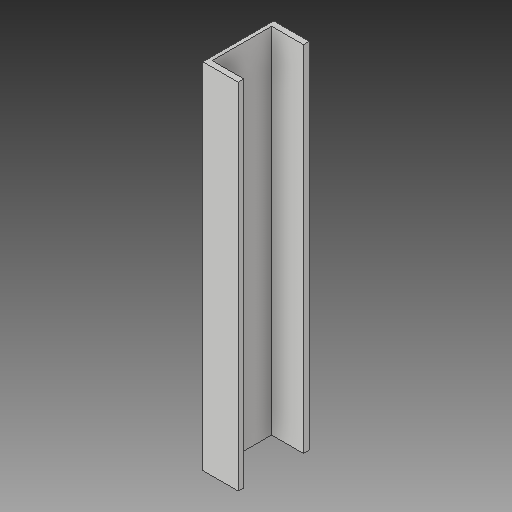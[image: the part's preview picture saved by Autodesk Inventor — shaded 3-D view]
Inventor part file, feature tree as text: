
AUTODESK INVENTOR PART (.ipt)
format: ipt  version: 2019 (Build 230136000, 136)  size: 88,576 bytes
history: native  units: mm
features: extrude x1, sketch x1
ambient origin geometry x8: Origin, YZ Plane, XZ Plane, XY Plane, X Axis, Y Axis, Z Axis, Center Point
bodies: Solid1 (feature_tree)
feature tree (2):
  extrude  "Extrusion1"  Depth=100.0mm
  sketch  "Sketch1"  dims[d0=50.0mm d1=100.0mm d2=8.0mm d3=45.0mm d4=84.0mm d5=500.0mm d6=0.0mm]
